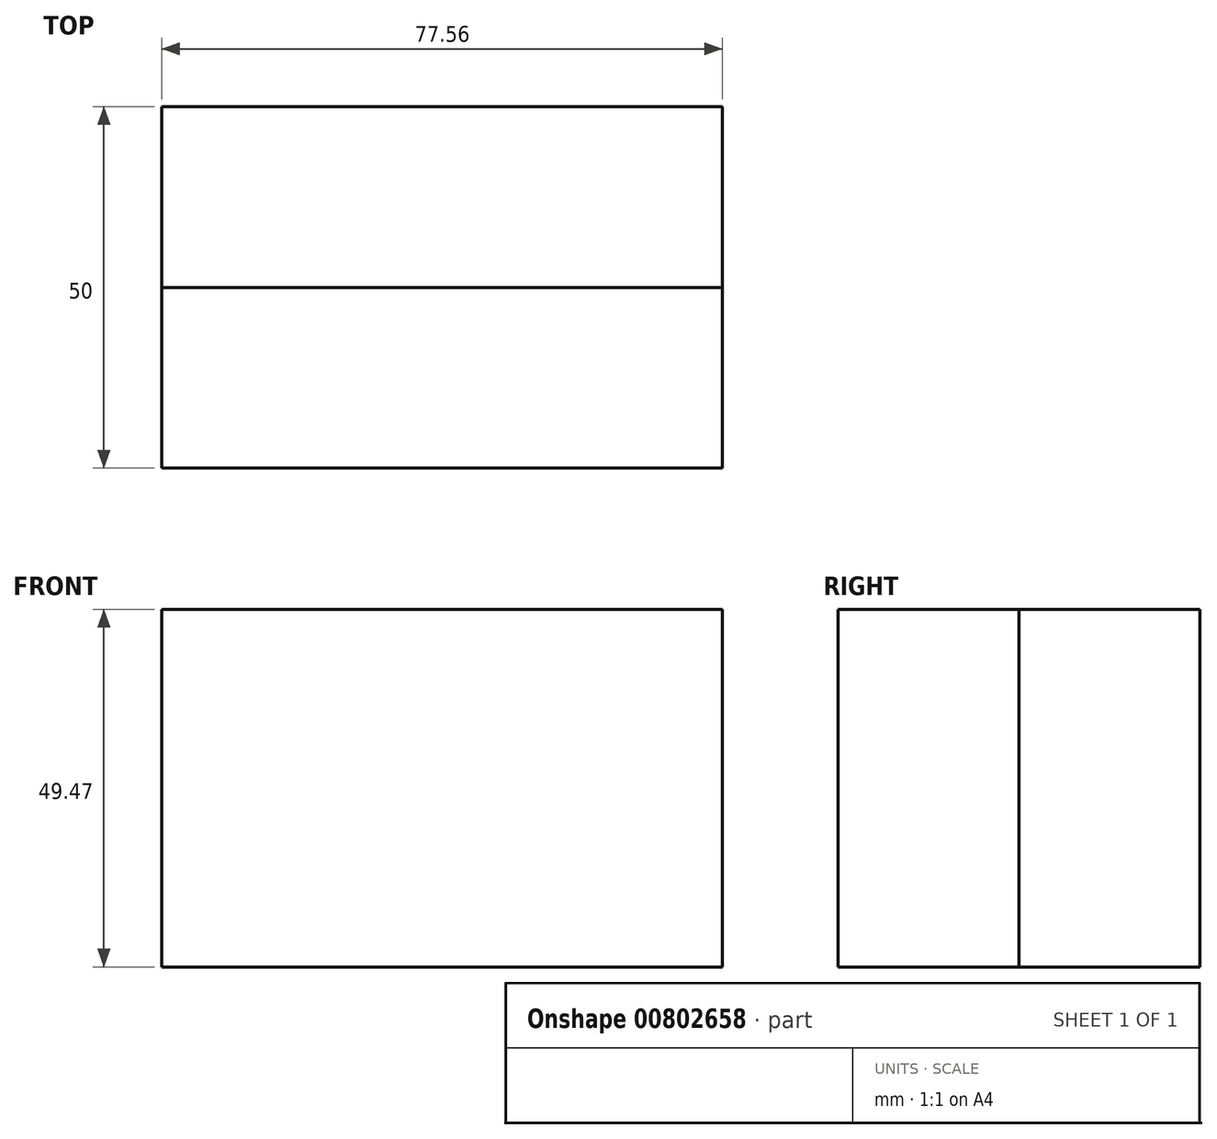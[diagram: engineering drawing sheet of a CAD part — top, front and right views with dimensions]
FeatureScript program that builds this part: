
annotation { "Feature Type Name" : "Feature", "Feature Type Description" : "" }
export const myFeature = defineFeature(function(context is Context, id is Id, definition is map)
    precondition{}
    {
        {
            var Q0;
            Q0=qCreatedBy(makeId("Front.planeOp"),FACE);
            var sketch = newSketch(context, id + "F0", { "sketchPlane" : qUnion([Q0])});
            skLineSegment(sketch, "E0.bottom", {"start": v(-111.06, 36.52) * mm, "end": v(-33.5, 36.52) * mm});
            skLineSegment(sketch, "E0.top", {"start": v(-111.06, -12.95) * mm, "end": v(-33.5, -12.95) * mm});
            skLineSegment(sketch, "E0.left", {"start": v(-111.06, 36.52) * mm, "end": v(-111.06, -12.95) * mm});
            skLineSegment(sketch, "E0.right", {"start": v(-33.5, 36.52) * mm, "end": v(-33.5, -12.95) * mm});
            skSolve(sketch);
        }
        {
            var Q0;
            Q0 = qSketchRegion(id + "F0", true);
            extrude(context, id + "F1", {"entities" : qUnion([Q0]), "depth" : 25 * mm, "offsetDistance" : 25 * mm});
        }
        {
            var Q0;
            Q0=makeQuery(id+"F1.opExtrude","SWEPT_BODY",BODY,{"disambiguationData":[OSD([sQuery(id+"F0.wireOp",EDGE,"E0.bottom"),sQuery(id+"F0.wireOp",EDGE,"E0.top"),sQuery(id+"F0.wireOp",EDGE,"E0.left"),sQuery(id+"F0.wireOp",EDGE,"E0.right")])]});
            var Q1;
            Q1=qCreatedBy(makeId("Front.planeOp"),FACE);
            mirror(context, id + "F2", {"entities" : qUnion([Q0]), "mirrorPlane" : qUnion([Q1])});
        }
    });
